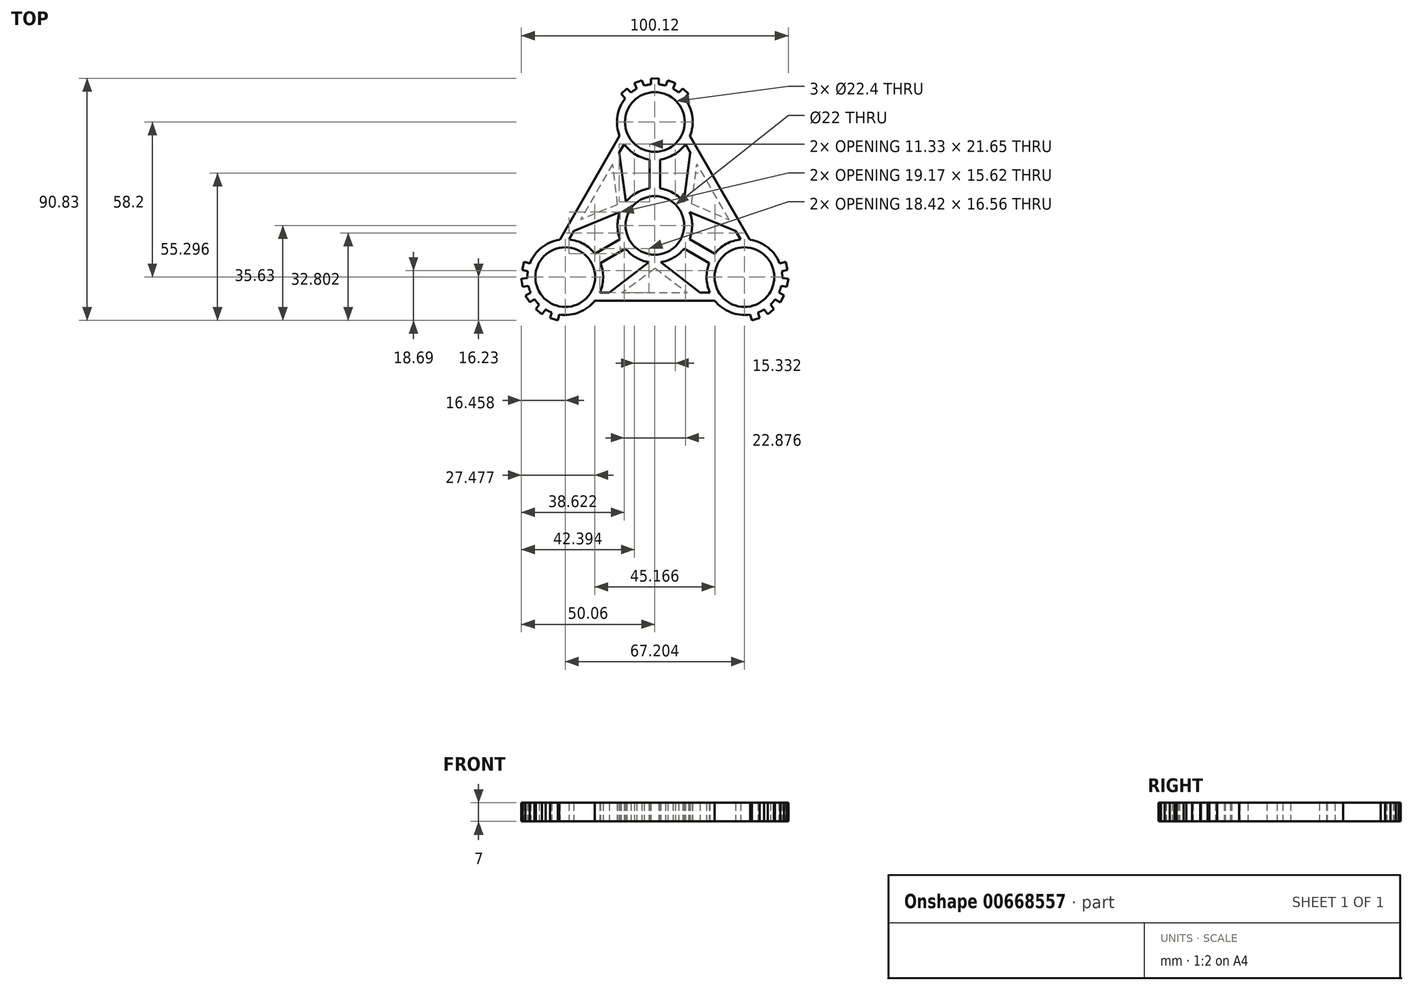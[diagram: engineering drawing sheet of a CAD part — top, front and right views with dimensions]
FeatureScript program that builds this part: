
annotation { "Feature Type Name" : "Feature", "Feature Type Description" : "" }
export const myFeature = defineFeature(function(context is Context, id is Id, definition is map)
    precondition{}
    {
        {
            var Q0;
            Q0=qCreatedBy(makeId("Top.planeOp"),FACE);
            var sketch = newSketch(context, id + "F0", { "sketchPlane" : qUnion([Q0])});
            skCircle(sketch, "E0", {"center": v(0, 0) * mm, "radius": 11 * mm});
            skArc(sketch, "E1.0", {"start": v(-2, 13.86) * mm, "mid": v(-6.9, 12.18) * mm, "end": v(-10.86, 8.84) * mm});
            skCircle(sketch, "E2", {"center": v(0, 38.8) * mm, "radius": 11.2 * mm});
            skArc(sketch, "E3.0", {"start": v(-11.05, 47.72) * mm, "mid": v(-14.04, 40.94) * mm, "end": v(-13.2, 33.57) * mm});
            skLineSegment(sketch, "E4", {"start": v(0, 11) * mm, "end": v(0, 27.6) * mm, "construction": true});
            skLineSegment(sketch, "E5.0", {"start": v(2, 13.86) * mm, "end": v(2, 24.74) * mm});
            skLineSegment(sketch, "E6.0", {"start": v(-2, 13.86) * mm, "end": v(-2, 24.74) * mm});
            skLineSegment(sketch, "E7", {"start": v(0, 53) * mm, "end": v(0, 55) * mm, "construction": true});
            skLineSegment(sketch, "E8.0", {"start": v(1.5, 52.92) * mm, "end": v(1.5, 55.2) * mm});
            skLineSegment(sketch, "E9.0", {"start": v(-1.5, 52.92) * mm, "end": v(-1.5, 55.05) * mm});
            skLineSegment(sketch, "E10", {"start": v(-1.5, 55.05) * mm, "end": v(1.5, 55.2) * mm});
            skLineSegment(sketch, "E11.1.0", {"start": v(4.83, 54.39) * mm, "end": v(7.66, 53.38) * mm});
            skLineSegment(sketch, "E11.1.1", {"start": v(4.02, 52.42) * mm, "end": v(4.83, 54.39) * mm});
            skLineSegment(sketch, "E11.1.2", {"start": v(6.79, 51.27) * mm, "end": v(7.66, 53.38) * mm});
            skLineSegment(sketch, "E11.2.0", {"start": v(10.43, 51.35) * mm, "end": v(12.66, 49.33) * mm});
            skLineSegment(sketch, "E11.2.1", {"start": v(8.92, 49.85) * mm, "end": v(10.43, 51.35) * mm});
            skLineSegment(sketch, "E11.2.2", {"start": v(11.05, 47.72) * mm, "end": v(12.66, 49.33) * mm});
            skLineSegment(sketch, "E11.anchor1", {"start": v(0, 38.8) * mm, "end": v(-1.5, 55.05) * mm, "construction": true});
            skLineSegment(sketch, "E11.anchor2", {"start": v(0, 38.8) * mm, "end": v(10.43, 51.35) * mm, "construction": true});
            skLineSegment(sketch, "E12.MirrorCS", {"start": v(-4.83, 54.39) * mm, "end": v(-7.66, 53.38) * mm});
            skLineSegment(sketch, "E13.MirrorCS", {"start": v(-4.02, 52.42) * mm, "end": v(-4.83, 54.39) * mm});
            skLineSegment(sketch, "E14.MirrorCS", {"start": v(-6.79, 51.27) * mm, "end": v(-7.66, 53.38) * mm});
            skLineSegment(sketch, "E15.MirrorCS", {"start": v(-8.92, 49.85) * mm, "end": v(-10.43, 51.35) * mm});
            skLineSegment(sketch, "E16.MirrorCS", {"start": v(-10.43, 51.35) * mm, "end": v(-12.66, 49.33) * mm});
            skLineSegment(sketch, "E17.MirrorCS", {"start": v(-11.05, 47.72) * mm, "end": v(-12.66, 49.33) * mm});
            skArc(sketch, "E18.trimOffspring", {"start": v(-6.79, 51.27) * mm, "mid": v(-7.89, 50.6) * mm, "end": v(-8.92, 49.85) * mm});
            skArc(sketch, "E19.trimOffspring", {"start": v(-1.3, 52.94) * mm, "mid": v(-2.67, 52.75) * mm, "end": v(-4.02, 52.42) * mm});
            skArc(sketch, "E20.trimOffspring", {"start": v(4.02, 52.42) * mm, "mid": v(2.77, 52.73) * mm, "end": v(1.5, 52.92) * mm});
            skArc(sketch, "E21.trimOffspring", {"start": v(9.08, 49.72) * mm, "mid": v(7.97, 50.55) * mm, "end": v(6.79, 51.27) * mm});
            skArc(sketch, "E22.trimOffspring", {"start": v(2, 24.74) * mm, "mid": v(7.34, 26.65) * mm, "end": v(11.52, 30.5) * mm});
            skLineSegment(sketch, "E23.1.0", {"start": v(-33.6, -19.4) * mm, "end": v(-46.92, -28.82) * mm, "construction": true});
            skPoint(sketch, "E23.1.1", {"position": v(-33.6, -19.4) * mm});
            skCircle(sketch, "E23.1.2", {"center": v(-33.6, -19.4) * mm, "radius": 11.2 * mm});
            skLineSegment(sketch, "E23.1.3", {"start": v(-9.53, -5.5) * mm, "end": v(-23.9, -13.8) * mm, "construction": true});
            skArc(sketch, "E23.1.4", {"start": v(-35.8, -33.43) * mm, "mid": v(-28.44, -32.63) * mm, "end": v(-22.47, -28.22) * mm});
            skLineSegment(sketch, "E23.1.5", {"start": v(-13, -5.2) * mm, "end": v(-22.43, -10.64) * mm});
            skLineSegment(sketch, "E23.1.6", {"start": v(-11, -8.66) * mm, "end": v(-20.43, -14.1) * mm});
            skLineSegment(sketch, "E23.1.7", {"start": v(-33.6, -19.4) * mm, "end": v(-49.69, -16.64) * mm, "construction": true});
            skArc(sketch, "E23.1.8", {"start": v(-22.43, -10.64) * mm, "mid": v(-26.75, -6.96) * mm, "end": v(-32.17, -5.27) * mm});
            skLineSegment(sketch, "E23.1.9", {"start": v(-41, -31.52) * mm, "end": v(-42.4, -33.32) * mm});
            skLineSegment(sketch, "E23.1.10", {"start": v(-35.8, -33.43) * mm, "end": v(-36.4, -35.63) * mm});
            skLineSegment(sketch, "E23.1.11", {"start": v(-49.69, -16.64) * mm, "end": v(-49.05, -13.7) * mm});
            skLineSegment(sketch, "E23.1.12", {"start": v(-47.8, -19.76) * mm, "end": v(-50.06, -20.05) * mm});
            skArc(sketch, "E23.1.13", {"start": v(-47.6, -17) * mm, "mid": v(-47.76, -18.37) * mm, "end": v(-47.8, -19.76) * mm});
            skLineSegment(sketch, "E23.1.14", {"start": v(-44.68, -31.38) * mm, "end": v(-42.4, -33.32) * mm});
            skLineSegment(sketch, "E23.1.15", {"start": v(-45.9, -26.5) * mm, "end": v(-47.63, -27.5) * mm, "construction": true});
            skLineSegment(sketch, "E23.1.16", {"start": v(-46.58, -25.16) * mm, "end": v(-48.55, -26.3) * mm});
            skLineSegment(sketch, "E23.1.17", {"start": v(-46.92, -28.82) * mm, "end": v(-48.55, -26.3) * mm});
            skLineSegment(sketch, "E23.1.18", {"start": v(-45.08, -27.76) * mm, "end": v(-46.92, -28.82) * mm});
            skLineSegment(sketch, "E23.1.19", {"start": v(-49.52, -23) * mm, "end": v(-50.06, -20.05) * mm});
            skLineSegment(sketch, "E23.1.20", {"start": v(-47.4, -22.73) * mm, "end": v(-49.52, -23) * mm});
            skArc(sketch, "E23.1.21", {"start": v(-47.4, -22.73) * mm, "mid": v(-47.05, -23.96) * mm, "end": v(-46.58, -25.16) * mm});
            skArc(sketch, "E23.1.22", {"start": v(-41, -31.52) * mm, "mid": v(-39.88, -32.14) * mm, "end": v(-38.7, -32.65) * mm});
            skLineSegment(sketch, "E23.1.23", {"start": v(-39.26, -34.7) * mm, "end": v(-36.4, -35.63) * mm});
            skLineSegment(sketch, "E23.1.24", {"start": v(-43.39, -29.69) * mm, "end": v(-44.68, -31.38) * mm});
            skLineSegment(sketch, "E23.1.25", {"start": v(-46.85, -14.3) * mm, "end": v(-49.05, -13.7) * mm});
            skArc(sketch, "E23.1.26", {"start": v(-45.2, -27.6) * mm, "mid": v(-44.34, -28.69) * mm, "end": v(-43.39, -29.69) * mm});
            skLineSegment(sketch, "E23.1.27", {"start": v(-38.7, -32.65) * mm, "end": v(-39.26, -34.7) * mm});
            skLineSegment(sketch, "E23.1.28", {"start": v(-47.63, -17.2) * mm, "end": v(-49.69, -16.64) * mm});
            skLineSegment(sketch, "E23.2.0", {"start": v(33.6, -19.4) * mm, "end": v(48.42, -26.23) * mm, "construction": true});
            skPoint(sketch, "E23.2.1", {"position": v(33.6, -19.4) * mm});
            skCircle(sketch, "E23.2.2", {"center": v(33.6, -19.4) * mm, "radius": 11.2 * mm});
            skLineSegment(sketch, "E23.2.3", {"start": v(9.53, -5.5) * mm, "end": v(23.9, -13.8) * mm, "construction": true});
            skArc(sketch, "E23.2.4", {"start": v(46.85, -14.3) * mm, "mid": v(42.47, -8.31) * mm, "end": v(35.68, -5.35) * mm});
            skLineSegment(sketch, "E23.2.5", {"start": v(11, -8.66) * mm, "end": v(20.43, -14.1) * mm});
            skLineSegment(sketch, "E23.2.6", {"start": v(13, -5.2) * mm, "end": v(22.43, -10.64) * mm});
            skLineSegment(sketch, "E23.2.7", {"start": v(33.6, -19.4) * mm, "end": v(39.26, -34.7) * mm, "construction": true});
            skArc(sketch, "E23.2.8", {"start": v(20.43, -14.1) * mm, "mid": v(19.4, -19.68) * mm, "end": v(20.65, -25.22) * mm});
            skLineSegment(sketch, "E23.2.9", {"start": v(47.8, -19.76) * mm, "end": v(50.06, -20.05) * mm});
            skLineSegment(sketch, "E23.2.10", {"start": v(46.85, -14.3) * mm, "end": v(49.05, -13.7) * mm});
            skLineSegment(sketch, "E23.2.11", {"start": v(39.26, -34.7) * mm, "end": v(36.4, -35.63) * mm});
            skLineSegment(sketch, "E23.2.12", {"start": v(41, -31.52) * mm, "end": v(42.4, -33.32) * mm});
            skArc(sketch, "E23.2.13", {"start": v(38.52, -32.72) * mm, "mid": v(39.8, -32.18) * mm, "end": v(41, -31.52) * mm});
            skLineSegment(sketch, "E23.2.14", {"start": v(49.52, -23) * mm, "end": v(50.06, -20.05) * mm});
            skLineSegment(sketch, "E23.2.15", {"start": v(45.9, -26.5) * mm, "end": v(47.63, -27.5) * mm, "construction": true});
            skLineSegment(sketch, "E23.2.16", {"start": v(45.08, -27.76) * mm, "end": v(47.05, -28.9) * mm});
            skLineSegment(sketch, "E23.2.17", {"start": v(48.42, -26.23) * mm, "end": v(47.05, -28.9) * mm});
            skLineSegment(sketch, "E23.2.18", {"start": v(46.58, -25.16) * mm, "end": v(48.42, -26.23) * mm});
            skLineSegment(sketch, "E23.2.19", {"start": v(44.68, -31.38) * mm, "end": v(42.4, -33.32) * mm});
            skLineSegment(sketch, "E23.2.20", {"start": v(43.39, -29.69) * mm, "end": v(44.68, -31.38) * mm});
            skArc(sketch, "E23.2.21", {"start": v(43.39, -29.69) * mm, "mid": v(44.28, -28.76) * mm, "end": v(45.08, -27.76) * mm});
            skArc(sketch, "E23.2.22", {"start": v(47.8, -19.76) * mm, "mid": v(47.77, -18.47) * mm, "end": v(47.63, -17.2) * mm});
            skLineSegment(sketch, "E23.2.23", {"start": v(49.69, -16.64) * mm, "end": v(49.05, -13.7) * mm});
            skLineSegment(sketch, "E23.2.24", {"start": v(47.4, -22.73) * mm, "end": v(49.52, -23) * mm});
            skLineSegment(sketch, "E23.2.25", {"start": v(35.8, -33.43) * mm, "end": v(36.4, -35.63) * mm});
            skArc(sketch, "E23.2.26", {"start": v(46.5, -25.34) * mm, "mid": v(47.02, -24.06) * mm, "end": v(47.4, -22.73) * mm});
            skLineSegment(sketch, "E23.2.27", {"start": v(47.63, -17.2) * mm, "end": v(49.69, -16.64) * mm});
            skLineSegment(sketch, "E23.2.28", {"start": v(38.7, -32.65) * mm, "end": v(39.26, -34.7) * mm});
            skArc(sketch, "E24.trimOffspring", {"start": v(13, -5.2) * mm, "mid": v(14, -0.11) * mm, "end": v(13.08, 4.98) * mm});
            skArc(sketch, "E25.trimOffspring", {"start": v(-11, -8.66) * mm, "mid": v(-7.1, -12.07) * mm, "end": v(-2.23, -13.82) * mm});
            skLineSegment(sketch, "E26", {"start": v(-13.2, 33.57) * mm, "end": v(-35.68, -5.35) * mm});
            skLineSegment(sketch, "E27.0", {"start": v(-11.52, 30.5) * mm, "end": v(-13.33, 27.35) * mm});
            skArc(sketch, "E28.trimOffspring", {"start": v(-11.52, 30.5) * mm, "mid": v(-7.34, 26.65) * mm, "end": v(-2, 24.74) * mm});
            skArc(sketch, "E29.trimOffspring", {"start": v(-35.68, -5.35) * mm, "mid": v(-42.47, -8.31) * mm, "end": v(-46.85, -14.3) * mm});
            skLineSegment(sketch, "E30", {"start": v(-12.12, 7) * mm, "end": v(-29.12, 0) * mm, "construction": true});
            skLineSegment(sketch, "E31", {"start": v(-12.12, 7) * mm, "end": v(-21.84, 12.61) * mm, "construction": true});
            skLineSegment(sketch, "E32.0", {"start": v(-13.97, 7.86) * mm, "end": v(-27.9, 2.13) * mm});
            skLineSegment(sketch, "E33.0", {"start": v(-13.08, 4.98) * mm, "end": v(-30.35, -2.13) * mm});
            skLineSegment(sketch, "E34.trimOffspring", {"start": v(-30.35, -2.13) * mm, "end": v(-32.17, -5.27) * mm});
            skArc(sketch, "E35.trimOffspring", {"start": v(-13.08, 4.98) * mm, "mid": v(-14, -0.11) * mm, "end": v(-13, -5.2) * mm});
            skLineSegment(sketch, "E36.MirrorCS", {"start": v(-10.86, 8.84) * mm, "end": v(-13.33, 27.35) * mm});
            skLineSegment(sketch, "E37.trimOffspring", {"start": v(-15.79, 23.1) * mm, "end": v(-27.9, 2.13) * mm});
            skPoint(sketch, "E38.orphan", {"position": v(-10.46, 9.3) * mm});
            skLineSegment(sketch, "E39.trimOffspring", {"start": v(-13.97, 7.86) * mm, "end": v(-15.79, 23.1) * mm});
            skPoint(sketch, "E40.MirrorCS.start.orphan", {"position": v(-13.3, 4.4) * mm});
            skLineSegment(sketch, "E41.1.0", {"start": v(-22.47, -28.22) * mm, "end": v(22.47, -28.22) * mm});
            skLineSegment(sketch, "E41.1.1", {"start": v(0.17, -16.03) * mm, "end": v(-12.1, -25.22) * mm});
            skLineSegment(sketch, "E41.1.2", {"start": v(0, -14) * mm, "end": v(0, -25.22) * mm, "construction": true});
            skLineSegment(sketch, "E41.1.3", {"start": v(-12.1, -25.22) * mm, "end": v(12.1, -25.22) * mm});
            skLineSegment(sketch, "E41.1.4", {"start": v(-2.23, -13.82) * mm, "end": v(-17.02, -25.22) * mm});
            skLineSegment(sketch, "E41.1.5", {"start": v(17.02, -25.22) * mm, "end": v(20.65, -25.22) * mm});
            skLineSegment(sketch, "E41.1.6", {"start": v(2.23, -13.82) * mm, "end": v(17.02, -25.22) * mm});
            skLineSegment(sketch, "E41.1.7", {"start": v(0.17, -16.03) * mm, "end": v(12.1, -25.22) * mm});
            skLineSegment(sketch, "E41.1.8", {"start": v(0, -14) * mm, "end": v(14.56, -25.22) * mm, "construction": true});
            skLineSegment(sketch, "E41.1.9", {"start": v(-20.65, -25.22) * mm, "end": v(-17.02, -25.22) * mm});
            skLineSegment(sketch, "E41.2.0", {"start": v(35.68, -5.35) * mm, "end": v(13.2, 33.57) * mm});
            skLineSegment(sketch, "E41.2.1", {"start": v(13.8, 8.16) * mm, "end": v(27.9, 2.13) * mm});
            skLineSegment(sketch, "E41.2.2", {"start": v(12.12, 7) * mm, "end": v(21.84, 12.61) * mm, "construction": true});
            skLineSegment(sketch, "E41.2.3", {"start": v(27.9, 2.13) * mm, "end": v(15.79, 23.1) * mm});
            skLineSegment(sketch, "E41.2.4", {"start": v(13.08, 4.98) * mm, "end": v(30.35, -2.13) * mm});
            skLineSegment(sketch, "E41.2.5", {"start": v(13.33, 27.35) * mm, "end": v(11.52, 30.5) * mm});
            skLineSegment(sketch, "E41.2.6", {"start": v(10.86, 8.84) * mm, "end": v(13.33, 27.35) * mm});
            skLineSegment(sketch, "E41.2.7", {"start": v(13.8, 8.16) * mm, "end": v(15.79, 23.1) * mm});
            skLineSegment(sketch, "E41.2.8", {"start": v(12.12, 7) * mm, "end": v(14.56, 25.22) * mm, "construction": true});
            skLineSegment(sketch, "E41.2.9", {"start": v(32.17, -5.27) * mm, "end": v(30.35, -2.13) * mm});
            skArc(sketch, "E42.trimOffspring", {"start": v(13.2, 33.57) * mm, "mid": v(14.04, 40.94) * mm, "end": v(11.05, 47.72) * mm});
            skArc(sketch, "E43.trimOffspring", {"start": v(32.17, -5.27) * mm, "mid": v(26.75, -6.96) * mm, "end": v(22.43, -10.64) * mm});
            skArc(sketch, "E44.trimOffspring", {"start": v(10.86, 8.84) * mm, "mid": v(6.9, 12.18) * mm, "end": v(2, 13.86) * mm});
            skArc(sketch, "E45.trimOffspring", {"start": v(2.23, -13.82) * mm, "mid": v(7.1, -12.07) * mm, "end": v(11, -8.66) * mm});
            skArc(sketch, "E46.trimOffspring", {"start": v(22.47, -28.22) * mm, "mid": v(28.44, -32.63) * mm, "end": v(35.8, -33.43) * mm});
            skArc(sketch, "E47.trimOffspring", {"start": v(-20.65, -25.22) * mm, "mid": v(-19.4, -19.68) * mm, "end": v(-20.43, -14.1) * mm});
            skSolve(sketch);
        }
        {
            var Q0;
            Q0=qSketchRegion(id+"F0",true);
            extrude(context, id + "F1", {"entities" : qUnion([Q0]), "depth" : 7 * mm});
        }
        {
            var Q0;
            Q0=makeQuery(id+"F1.opExtrude","CAP_FACE",FACE,{"disambiguationData":[OSD([sQuery(id+"F0.wireOp",EDGE,"E0"),sQuery(id+"F0.wireOp",EDGE,"E1.0"),sQuery(id+"F0.wireOp",EDGE,"E2"),sQuery(id+"F0.wireOp",EDGE,"E3.0"),sQuery(id+"F0.wireOp",EDGE,"E5.0"),sQuery(id+"F0.wireOp",EDGE,"E6.0"),sQuery(id+"F0.wireOp",EDGE,"E8.0"),sQuery(id+"F0.wireOp",EDGE,"E9.0"),sQuery(id+"F0.wireOp",EDGE,"E10"),sQuery(id+"F0.wireOp",EDGE,"E11.1.0"),sQuery(id+"F0.wireOp",EDGE,"E11.1.1"),sQuery(id+"F0.wireOp",EDGE,"E11.1.2"),sQuery(id+"F0.wireOp",EDGE,"E11.2.0"),sQuery(id+"F0.wireOp",EDGE,"E11.2.1"),sQuery(id+"F0.wireOp",EDGE,"E11.2.2"),sQuery(id+"F0.wireOp",EDGE,"E12.MirrorCS"),sQuery(id+"F0.wireOp",EDGE,"E13.MirrorCS"),sQuery(id+"F0.wireOp",EDGE,"E14.MirrorCS"),sQuery(id+"F0.wireOp",EDGE,"E15.MirrorCS"),sQuery(id+"F0.wireOp",EDGE,"E16.MirrorCS"),sQuery(id+"F0.wireOp",EDGE,"E17.MirrorCS"),sQuery(id+"F0.wireOp",EDGE,"E18.trimOffspring"),sQuery(id+"F0.wireOp",EDGE,"E19.trimOffspring"),sQuery(id+"F0.wireOp",EDGE,"E20.trimOffspring"),sQuery(id+"F0.wireOp",EDGE,"E21.trimOffspring"),sQuery(id+"F0.wireOp",EDGE,"E22.trimOffspring"),sQuery(id+"F0.wireOp",EDGE,"E23.1.2"),sQuery(id+"F0.wireOp",EDGE,"E23.1.4"),sQuery(id+"F0.wireOp",EDGE,"E23.1.5"),sQuery(id+"F0.wireOp",EDGE,"E23.1.6"),sQuery(id+"F0.wireOp",EDGE,"E23.1.8"),sQuery(id+"F0.wireOp",EDGE,"E23.1.9"),sQuery(id+"F0.wireOp",EDGE,"E23.1.10"),sQuery(id+"F0.wireOp",EDGE,"E23.1.11"),sQuery(id+"F0.wireOp",EDGE,"E23.1.12"),sQuery(id+"F0.wireOp",EDGE,"E23.1.13"),sQuery(id+"F0.wireOp",EDGE,"E23.1.14"),sQuery(id+"F0.wireOp",EDGE,"E23.1.16"),sQuery(id+"F0.wireOp",EDGE,"E23.1.17"),sQuery(id+"F0.wireOp",EDGE,"E23.1.18"),sQuery(id+"F0.wireOp",EDGE,"E23.1.19"),sQuery(id+"F0.wireOp",EDGE,"E23.1.20"),sQuery(id+"F0.wireOp",EDGE,"E23.1.21"),sQuery(id+"F0.wireOp",EDGE,"E23.1.22"),sQuery(id+"F0.wireOp",EDGE,"E23.1.23"),sQuery(id+"F0.wireOp",EDGE,"E23.1.24"),sQuery(id+"F0.wireOp",EDGE,"E23.1.25"),sQuery(id+"F0.wireOp",EDGE,"E23.1.26"),sQuery(id+"F0.wireOp",EDGE,"E23.1.27"),sQuery(id+"F0.wireOp",EDGE,"E23.1.28"),sQuery(id+"F0.wireOp",EDGE,"E23.2.2"),sQuery(id+"F0.wireOp",EDGE,"E23.2.4"),sQuery(id+"F0.wireOp",EDGE,"E23.2.5"),sQuery(id+"F0.wireOp",EDGE,"E23.2.6"),sQuery(id+"F0.wireOp",EDGE,"E23.2.8"),sQuery(id+"F0.wireOp",EDGE,"E23.2.9"),sQuery(id+"F0.wireOp",EDGE,"E23.2.10"),sQuery(id+"F0.wireOp",EDGE,"E23.2.11"),sQuery(id+"F0.wireOp",EDGE,"E23.2.12"),sQuery(id+"F0.wireOp",EDGE,"E23.2.13"),sQuery(id+"F0.wireOp",EDGE,"E23.2.14"),sQuery(id+"F0.wireOp",EDGE,"E23.2.16"),sQuery(id+"F0.wireOp",EDGE,"E23.2.17"),sQuery(id+"F0.wireOp",EDGE,"E23.2.18"),sQuery(id+"F0.wireOp",EDGE,"E23.2.19"),sQuery(id+"F0.wireOp",EDGE,"E23.2.20"),sQuery(id+"F0.wireOp",EDGE,"E23.2.21"),sQuery(id+"F0.wireOp",EDGE,"E23.2.22"),sQuery(id+"F0.wireOp",EDGE,"E23.2.23"),sQuery(id+"F0.wireOp",EDGE,"E23.2.24"),sQuery(id+"F0.wireOp",EDGE,"E23.2.25"),sQuery(id+"F0.wireOp",EDGE,"E23.2.26"),sQuery(id+"F0.wireOp",EDGE,"E23.2.27"),sQuery(id+"F0.wireOp",EDGE,"E23.2.28"),sQuery(id+"F0.wireOp",EDGE,"E24.trimOffspring"),sQuery(id+"F0.wireOp",EDGE,"E25.trimOffspring"),sQuery(id+"F0.wireOp",EDGE,"E26"),sQuery(id+"F0.wireOp",EDGE,"E27.0"),sQuery(id+"F0.wireOp",EDGE,"E28.trimOffspring"),sQuery(id+"F0.wireOp",EDGE,"E29.trimOffspring"),sQuery(id+"F0.wireOp",EDGE,"E32.0"),sQuery(id+"F0.wireOp",EDGE,"E33.0"),sQuery(id+"F0.wireOp",EDGE,"E34.trimOffspring"),sQuery(id+"F0.wireOp",EDGE,"E35.trimOffspring"),sQuery(id+"F0.wireOp",EDGE,"E36.MirrorCS"),sQuery(id+"F0.wireOp",EDGE,"E37.trimOffspring"),sQuery(id+"F0.wireOp",EDGE,"E39.trimOffspring"),sQuery(id+"F0.wireOp",EDGE,"E41.1.0"),sQuery(id+"F0.wireOp",EDGE,"E41.1.1"),sQuery(id+"F0.wireOp",EDGE,"E41.1.3"),sQuery(id+"F0.wireOp",EDGE,"E41.1.4"),sQuery(id+"F0.wireOp",EDGE,"E41.1.5"),sQuery(id+"F0.wireOp",EDGE,"E41.1.6"),sQuery(id+"F0.wireOp",EDGE,"E41.1.7"),sQuery(id+"F0.wireOp",EDGE,"E41.1.9"),sQuery(id+"F0.wireOp",EDGE,"E41.2.0"),sQuery(id+"F0.wireOp",EDGE,"E41.2.1"),sQuery(id+"F0.wireOp",EDGE,"E41.2.3"),sQuery(id+"F0.wireOp",EDGE,"E41.2.4"),sQuery(id+"F0.wireOp",EDGE,"E41.2.5"),sQuery(id+"F0.wireOp",EDGE,"E41.2.6"),sQuery(id+"F0.wireOp",EDGE,"E41.2.7"),sQuery(id+"F0.wireOp",EDGE,"E41.2.9"),sQuery(id+"F0.wireOp",EDGE,"E42.trimOffspring"),sQuery(id+"F0.wireOp",EDGE,"E43.trimOffspring"),sQuery(id+"F0.wireOp",EDGE,"E44.trimOffspring"),sQuery(id+"F0.wireOp",EDGE,"E45.trimOffspring"),sQuery(id+"F0.wireOp",EDGE,"E46.trimOffspring"),sQuery(id+"F0.wireOp",EDGE,"E47.trimOffspring")])],"isStart":false});
            var sketch = newSketch(context, id + "F2", { "sketchPlane" : qUnion([Q0])});
            skLineSegment(sketch, "E48", {"start": v(15.79, 23.1) * mm, "end": v(27.9, 2.13) * mm});
            skLineSegment(sketch, "E49", {"start": v(27.9, 2.13) * mm, "end": v(13.8, 8.16) * mm});
            skLineSegment(sketch, "E50", {"start": v(13.8, 8.16) * mm, "end": v(15.79, 23.1) * mm});
            skLineSegment(sketch, "E51", {"start": v(-15.79, 23.1) * mm, "end": v(-13.97, 7.86) * mm});
            skLineSegment(sketch, "E52", {"start": v(-13.97, 7.86) * mm, "end": v(-27.9, 2.13) * mm});
            skLineSegment(sketch, "E53", {"start": v(-27.9, 2.13) * mm, "end": v(-15.79, 23.1) * mm});
            skLineSegment(sketch, "E54", {"start": v(12.1, -25.22) * mm, "end": v(0.17, -16.03) * mm});
            skLineSegment(sketch, "E55", {"start": v(0.17, -16.03) * mm, "end": v(-11.52, -24.78) * mm});
            skLineSegment(sketch, "E56", {"start": v(-11.52, -24.78) * mm, "end": v(-12.1, -25.22) * mm});
            skLineSegment(sketch, "E57", {"start": v(-12.1, -25.22) * mm, "end": v(0.17, -16.03) * mm});
            skLineSegment(sketch, "E58", {"start": v(12.1, -25.22) * mm, "end": v(-12.1, -25.22) * mm});
            skSolve(sketch);
        }
        {
            var Q0;
            Q0=makeQuery(id+"F2.imprint","IMPRINT",FACE,{"disambiguationData":[TD([[makeQuery(id+"F2.imprint","IMPRINT",EDGE,{"derivedFrom":sQuery(id+"F2.wireOp",EDGE,"E48")}),1.0]])]});
            var Q1;
            Q1=makeQuery(id+"F2.imprint","IMPRINT",FACE,{"disambiguationData":[TD([[makeQuery(id+"F2.imprint","IMPRINT",EDGE,{"derivedFrom":sQuery(id+"F2.wireOp",EDGE,"E54")}),-1.0]])]});
            var Q2;
            Q2=makeQuery(id+"F2.imprint","IMPRINT",FACE,{"disambiguationData":[TD([[makeQuery(id+"F2.imprint","IMPRINT",EDGE,{"derivedFrom":sQuery(id+"F2.wireOp",EDGE,"E51")}),1.0]])]});
            extrude(context, id + "F3", {"entities" : qUnion([Q0, Q1, Q2]), "operationType" : NewBodyOperationType.ADD, "oppositeDirection" : true, "depth" : 6.8 * mm, "offsetDistance" : 25 * mm});
        }
    });
